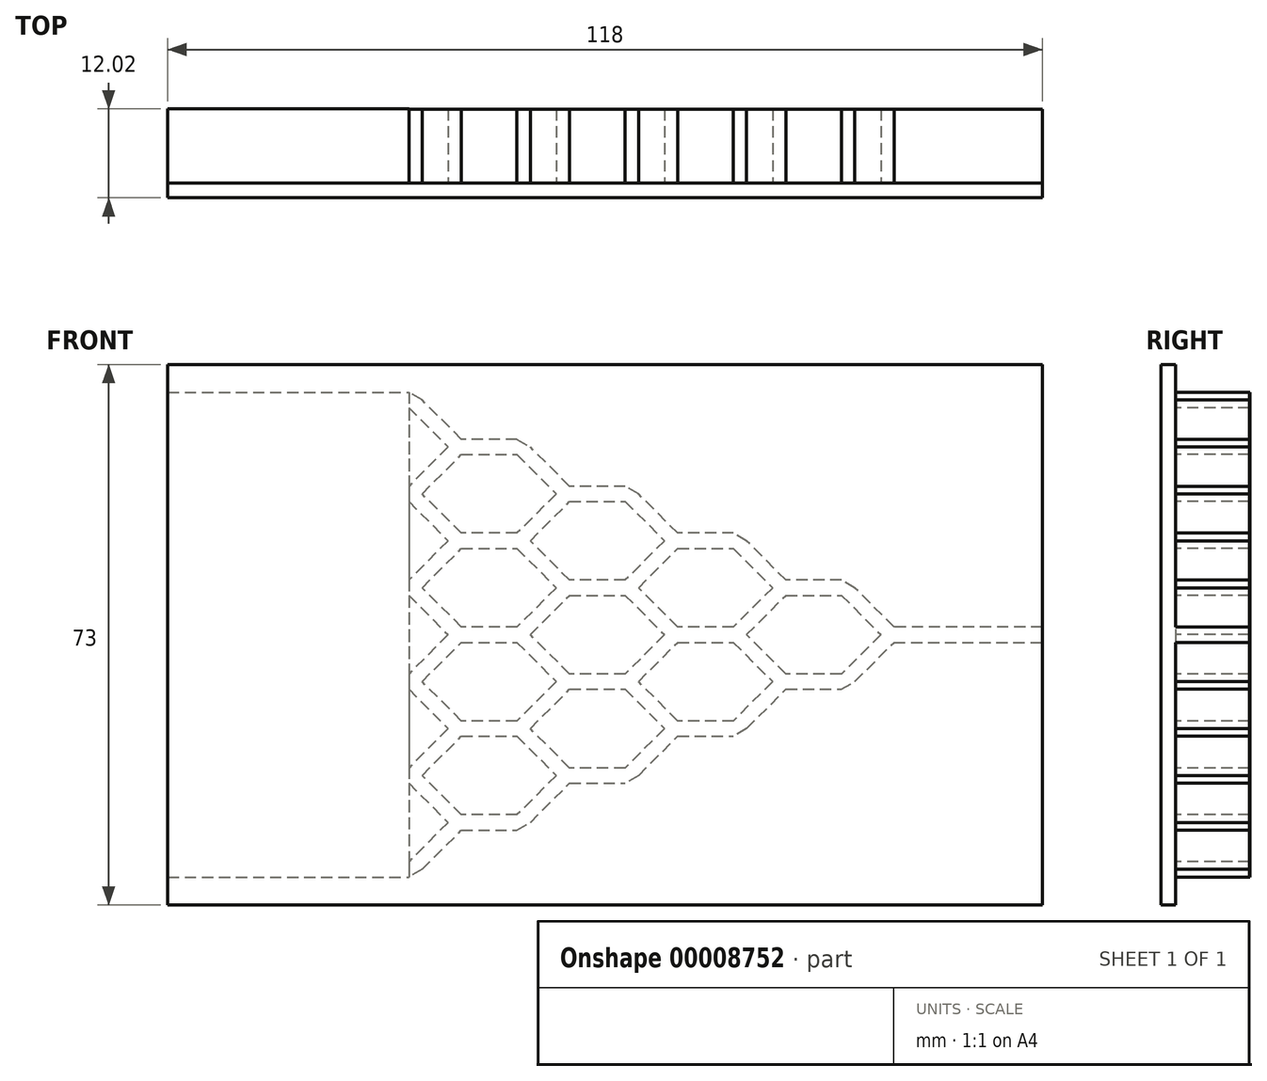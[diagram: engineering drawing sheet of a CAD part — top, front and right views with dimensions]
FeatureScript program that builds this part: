
annotation { "Feature Type Name" : "Feature", "Feature Type Description" : "" }
export const myFeature = defineFeature(function(context is Context, id is Id, definition is map)
    precondition{}
    {
        {
            var Q0;
            Q0=qCreatedBy(makeId("Front.planeOp"),FACE);
            var sketch = newSketch(context, id + "F0", { "sketchPlane" : qUnion([Q0])});
            skLineSegment(sketch, "E0.bottom", {"start": v(-59, 36.5) * mm, "end": v(59, 36.5) * mm});
            skLineSegment(sketch, "E0.top", {"start": v(-59, -36.5) * mm, "end": v(59, -36.5) * mm});
            skLineSegment(sketch, "E0.left", {"start": v(-59, 36.5) * mm, "end": v(-59, -36.5) * mm});
            skLineSegment(sketch, "E0.right", {"start": v(59, 36.5) * mm, "end": v(59, -36.5) * mm});
            skSolve(sketch);
        }
        {
            var Q0;
            Q0 = qSketchRegion(id + "F0", true);
            extrude(context, id + "F1", {"entities" : qUnion([Q0]), "depth" : 2 * mm});
        }
        {
            var Q0;
            Q0=makeQuery(id+"F1.opExtrude","CAP_FACE",FACE,{"disambiguationData":[OSD([sQuery(id+"F0.wireOp",EDGE,"E0.bottom"),sQuery(id+"F0.wireOp",EDGE,"E0.top"),sQuery(id+"F0.wireOp",EDGE,"E0.left"),sQuery(id+"F0.wireOp",EDGE,"E0.right")])],"isStart":true});
            var sketch = newSketch(context, id + "F2", { "sketchPlane" : qUnion([Q0])});
            skLineSegment(sketch, "E1", {"start": v(-59, 1.04) * mm, "end": v(-39, 1.04) * mm});
            skLineSegment(sketch, "E2", {"start": v(-39, 1.04) * mm, "end": v(-33.7, 6.34) * mm});
            skLineSegment(sketch, "E3", {"start": v(-31.9, 5.3) * mm, "end": v(-37.2, 0) * mm});
            skLineSegment(sketch, "E4", {"start": v(-37.2, 0) * mm, "end": v(-31.9, -5.3) * mm});
            skLineSegment(sketch, "E5", {"start": v(-33.7, -6.34) * mm, "end": v(-39, -1.04) * mm});
            skLineSegment(sketch, "E6", {"start": v(-39, -1.04) * mm, "end": v(-59, -1.04) * mm});
            skLineSegment(sketch, "E7", {"start": v(22.8, 0) * mm, "end": v(-82.74, 0) * mm, "construction": true});
            skLineSegment(sketch, "E8", {"start": v(-39, 1.04) * mm, "end": v(-37.2, 0) * mm, "construction": true});
            skLineSegment(sketch, "E9", {"start": v(-37.2, 0) * mm, "end": v(-39, -1.04) * mm, "construction": true});
            skLineSegment(sketch, "E10", {"start": v(-39, 1.04) * mm, "end": v(-39, -1.04) * mm, "construction": true});
            skLineSegment(sketch, "E11", {"start": v(-31.9, 5.3) * mm, "end": v(-33.7, 6.34) * mm, "construction": true});
            skLineSegment(sketch, "E12", {"start": v(-31.9, -5.3) * mm, "end": v(-33.7, -6.34) * mm, "construction": true});
            skLineSegment(sketch, "E13", {"start": v(23.45, 0) * mm, "end": v(-32.5, 0) * mm, "construction": true});
            skLineSegment(sketch, "E14", {"start": v(-59, 1.04) * mm, "end": v(-59, -1.04) * mm, "construction": true});
            skLineSegment(sketch, "E15", {"start": v(-31.9, 7.37) * mm, "end": v(-24.4, 7.37) * mm});
            skLineSegment(sketch, "E16", {"start": v(-24.4, 7.37) * mm, "end": v(-19.1, 12.68) * mm});
            skLineSegment(sketch, "E17", {"start": v(-17.3, 11.64) * mm, "end": v(-22.61, 6.34) * mm});
            skLineSegment(sketch, "E18", {"start": v(-22.61, 6.34) * mm, "end": v(-17.3, 1.04) * mm});
            skLineSegment(sketch, "E19", {"start": v(-19.1, 0) * mm, "end": v(-24.4, 5.3) * mm});
            skLineSegment(sketch, "E20", {"start": v(-24.4, 5.3) * mm, "end": v(-31.9, 5.3) * mm});
            skLineSegment(sketch, "E21", {"start": v(-24.4, 7.37) * mm, "end": v(-22.61, 6.34) * mm, "construction": true});
            skLineSegment(sketch, "E22", {"start": v(-22.61, 6.34) * mm, "end": v(-24.4, 5.3) * mm, "construction": true});
            skLineSegment(sketch, "E23", {"start": v(-24.4, 7.37) * mm, "end": v(-24.4, 5.3) * mm, "construction": true});
            skLineSegment(sketch, "E24", {"start": v(-17.3, 11.64) * mm, "end": v(-19.1, 12.68) * mm, "construction": true});
            skLineSegment(sketch, "E25", {"start": v(-17.3, 1.04) * mm, "end": v(-19.1, 0) * mm, "construction": true});
            skLineSegment(sketch, "E26", {"start": v(-31.9, -5.3) * mm, "end": v(-24.4, -5.3) * mm});
            skLineSegment(sketch, "E27", {"start": v(-24.4, -5.3) * mm, "end": v(-19.1, 0) * mm});
            skLineSegment(sketch, "E28", {"start": v(-17.3, -1.04) * mm, "end": v(-22.61, -6.34) * mm});
            skLineSegment(sketch, "E29", {"start": v(-22.61, -6.34) * mm, "end": v(-17.3, -11.64) * mm});
            skLineSegment(sketch, "E30", {"start": v(-19.1, -12.68) * mm, "end": v(-24.4, -7.37) * mm});
            skLineSegment(sketch, "E31", {"start": v(-24.4, -7.37) * mm, "end": v(-31.9, -7.37) * mm});
            skLineSegment(sketch, "E32", {"start": v(22.76, -6.34) * mm, "end": v(-25.18, -6.34) * mm, "construction": true});
            skLineSegment(sketch, "E33", {"start": v(-24.4, -5.3) * mm, "end": v(-22.61, -6.34) * mm, "construction": true});
            skLineSegment(sketch, "E34", {"start": v(-22.61, -6.34) * mm, "end": v(-24.4, -7.37) * mm, "construction": true});
            skLineSegment(sketch, "E35", {"start": v(-24.4, -5.3) * mm, "end": v(-24.4, -7.37) * mm, "construction": true});
            skLineSegment(sketch, "E36", {"start": v(-17.3, -1.04) * mm, "end": v(-19.1, 0) * mm, "construction": true});
            skLineSegment(sketch, "E37", {"start": v(-17.3, -11.64) * mm, "end": v(-19.1, -12.68) * mm, "construction": true});
            skLineSegment(sketch, "E38", {"start": v(-17.3, 13.71) * mm, "end": v(-9.8, 13.71) * mm});
            skLineSegment(sketch, "E39", {"start": v(-9.8, 13.71) * mm, "end": v(-4.5, 19.02) * mm});
            skLineSegment(sketch, "E40", {"start": v(-2.71, 17.98) * mm, "end": v(-8.01, 12.68) * mm});
            skLineSegment(sketch, "E41", {"start": v(-8.01, 12.68) * mm, "end": v(-2.71, 7.37) * mm});
            skLineSegment(sketch, "E42", {"start": v(-4.5, 6.34) * mm, "end": v(-9.8, 11.64) * mm});
            skLineSegment(sketch, "E43", {"start": v(-9.8, 11.64) * mm, "end": v(-17.3, 11.64) * mm});
            skLineSegment(sketch, "E44", {"start": v(19.34, 12.68) * mm, "end": v(-28.6, 12.68) * mm, "construction": true});
            skLineSegment(sketch, "E45", {"start": v(-9.8, 13.71) * mm, "end": v(-8.01, 12.68) * mm, "construction": true});
            skLineSegment(sketch, "E46", {"start": v(-8.01, 12.68) * mm, "end": v(-9.8, 11.64) * mm, "construction": true});
            skLineSegment(sketch, "E47", {"start": v(-9.8, 13.71) * mm, "end": v(-9.8, 11.64) * mm, "construction": true});
            skLineSegment(sketch, "E48", {"start": v(-2.71, 17.98) * mm, "end": v(-4.5, 19.02) * mm, "construction": true});
            skLineSegment(sketch, "E49", {"start": v(-2.71, 7.37) * mm, "end": v(-4.5, 6.34) * mm, "construction": true});
            skLineSegment(sketch, "E50", {"start": v(-17.3, 1.04) * mm, "end": v(-9.8, 1.04) * mm});
            skLineSegment(sketch, "E51", {"start": v(-9.8, 1.04) * mm, "end": v(-4.5, 6.34) * mm});
            skLineSegment(sketch, "E52", {"start": v(-2.71, 5.3) * mm, "end": v(-8.01, 0) * mm});
            skLineSegment(sketch, "E53", {"start": v(-8.01, 0) * mm, "end": v(-2.71, -5.3) * mm});
            skLineSegment(sketch, "E54", {"start": v(-4.5, -6.34) * mm, "end": v(-9.8, -1.04) * mm});
            skLineSegment(sketch, "E55", {"start": v(-9.8, -1.04) * mm, "end": v(-17.3, -1.04) * mm});
            skLineSegment(sketch, "E56", {"start": v(23.63, 0) * mm, "end": v(-24.3, 0) * mm, "construction": true});
            skLineSegment(sketch, "E57", {"start": v(-9.8, 1.04) * mm, "end": v(-8.01, 0) * mm, "construction": true});
            skLineSegment(sketch, "E58", {"start": v(-8.01, 0) * mm, "end": v(-9.8, -1.04) * mm, "construction": true});
            skLineSegment(sketch, "E59", {"start": v(-9.8, 1.04) * mm, "end": v(-9.8, -1.04) * mm, "construction": true});
            skLineSegment(sketch, "E60", {"start": v(-2.71, 5.3) * mm, "end": v(-4.5, 6.34) * mm, "construction": true});
            skLineSegment(sketch, "E61", {"start": v(-2.71, -5.3) * mm, "end": v(-4.5, -6.34) * mm, "construction": true});
            skLineSegment(sketch, "E62", {"start": v(-17.3, -11.64) * mm, "end": v(-9.8, -11.64) * mm});
            skLineSegment(sketch, "E63", {"start": v(-9.8, -11.64) * mm, "end": v(-4.5, -6.34) * mm});
            skLineSegment(sketch, "E64", {"start": v(-2.71, -7.37) * mm, "end": v(-8.01, -12.68) * mm});
            skLineSegment(sketch, "E65", {"start": v(-8.01, -12.68) * mm, "end": v(-2.71, -17.98) * mm});
            skLineSegment(sketch, "E66", {"start": v(-4.5, -19.02) * mm, "end": v(-9.8, -13.71) * mm});
            skLineSegment(sketch, "E67", {"start": v(-9.8, -13.71) * mm, "end": v(-17.3, -13.71) * mm});
            skLineSegment(sketch, "E68", {"start": v(17.06, -12.68) * mm, "end": v(-30.88, -12.68) * mm, "construction": true});
            skLineSegment(sketch, "E69", {"start": v(-9.8, -11.64) * mm, "end": v(-8.01, -12.68) * mm, "construction": true});
            skLineSegment(sketch, "E70", {"start": v(-8.01, -12.68) * mm, "end": v(-9.8, -13.71) * mm, "construction": true});
            skLineSegment(sketch, "E71", {"start": v(-9.8, -11.64) * mm, "end": v(-9.8, -13.71) * mm, "construction": true});
            skLineSegment(sketch, "E72", {"start": v(-2.71, -7.37) * mm, "end": v(-4.5, -6.34) * mm, "construction": true});
            skLineSegment(sketch, "E73", {"start": v(-2.71, -17.98) * mm, "end": v(-4.5, -19.02) * mm, "construction": true});
            skLineSegment(sketch, "E74", {"start": v(-31.9, -7.37) * mm, "end": v(-33.7, -6.34) * mm});
            skLineSegment(sketch, "E75", {"start": v(-2.71, 20.05) * mm, "end": v(4.79, 20.05) * mm});
            skLineSegment(sketch, "E76", {"start": v(4.79, 20.05) * mm, "end": v(10.1, 25.35) * mm});
            skLineSegment(sketch, "E77", {"start": v(11.89, 24.32) * mm, "end": v(6.58, 19.02) * mm});
            skLineSegment(sketch, "E78", {"start": v(6.58, 19.02) * mm, "end": v(11.89, 13.71) * mm});
            skLineSegment(sketch, "E79", {"start": v(10.1, 12.68) * mm, "end": v(4.79, 17.98) * mm});
            skLineSegment(sketch, "E80", {"start": v(4.79, 17.98) * mm, "end": v(-2.71, 17.98) * mm});
            skLineSegment(sketch, "E81", {"start": v(36.18, 19.02) * mm, "end": v(-11.76, 19.02) * mm, "construction": true});
            skLineSegment(sketch, "E82", {"start": v(4.79, 20.05) * mm, "end": v(6.58, 19.02) * mm, "construction": true});
            skLineSegment(sketch, "E83", {"start": v(6.58, 19.02) * mm, "end": v(4.79, 17.98) * mm, "construction": true});
            skLineSegment(sketch, "E84", {"start": v(4.79, 20.05) * mm, "end": v(4.79, 17.98) * mm, "construction": true});
            skLineSegment(sketch, "E85", {"start": v(11.89, 24.32) * mm, "end": v(10.1, 25.35) * mm, "construction": true});
            skLineSegment(sketch, "E86", {"start": v(11.89, 13.71) * mm, "end": v(10.1, 12.68) * mm, "construction": true});
            skLineSegment(sketch, "E87", {"start": v(-2.71, -17.98) * mm, "end": v(4.79, -17.98) * mm});
            skLineSegment(sketch, "E88", {"start": v(4.79, -17.98) * mm, "end": v(10.1, -12.68) * mm});
            skLineSegment(sketch, "E89", {"start": v(11.89, -13.71) * mm, "end": v(6.58, -19.02) * mm});
            skLineSegment(sketch, "E90", {"start": v(6.58, -19.02) * mm, "end": v(11.89, -24.32) * mm});
            skLineSegment(sketch, "E91", {"start": v(10.1, -25.35) * mm, "end": v(4.79, -20.05) * mm});
            skLineSegment(sketch, "E92", {"start": v(4.79, -20.05) * mm, "end": v(-2.71, -20.05) * mm});
            skLineSegment(sketch, "E93", {"start": v(31.97, -19.02) * mm, "end": v(-15.97, -19.02) * mm, "construction": true});
            skLineSegment(sketch, "E94", {"start": v(4.79, -17.98) * mm, "end": v(6.58, -19.02) * mm, "construction": true});
            skLineSegment(sketch, "E95", {"start": v(6.58, -19.02) * mm, "end": v(4.79, -20.05) * mm, "construction": true});
            skLineSegment(sketch, "E96", {"start": v(4.79, -17.98) * mm, "end": v(4.79, -20.05) * mm, "construction": true});
            skLineSegment(sketch, "E97", {"start": v(11.89, -13.71) * mm, "end": v(10.1, -12.68) * mm, "construction": true});
            skLineSegment(sketch, "E98", {"start": v(11.89, -24.32) * mm, "end": v(10.1, -25.35) * mm, "construction": true});
            skLineSegment(sketch, "E99", {"start": v(-2.71, 7.37) * mm, "end": v(4.79, 7.37) * mm});
            skLineSegment(sketch, "E100", {"start": v(4.79, 7.37) * mm, "end": v(10.1, 12.68) * mm});
            skLineSegment(sketch, "E101", {"start": v(11.89, 11.64) * mm, "end": v(6.58, 6.34) * mm});
            skLineSegment(sketch, "E102", {"start": v(6.58, 6.34) * mm, "end": v(11.89, 1.04) * mm});
            skLineSegment(sketch, "E103", {"start": v(10.1, 0) * mm, "end": v(4.79, 5.3) * mm});
            skLineSegment(sketch, "E104", {"start": v(4.79, 5.3) * mm, "end": v(-2.71, 5.3) * mm});
            skLineSegment(sketch, "E105", {"start": v(22.04, 6.34) * mm, "end": v(-25.9, 6.34) * mm, "construction": true});
            skLineSegment(sketch, "E106", {"start": v(4.79, 7.37) * mm, "end": v(6.58, 6.34) * mm, "construction": true});
            skLineSegment(sketch, "E107", {"start": v(6.58, 6.34) * mm, "end": v(4.79, 5.3) * mm, "construction": true});
            skLineSegment(sketch, "E108", {"start": v(4.79, 7.37) * mm, "end": v(4.79, 5.3) * mm, "construction": true});
            skLineSegment(sketch, "E109", {"start": v(11.89, 11.64) * mm, "end": v(10.1, 12.68) * mm, "construction": true});
            skLineSegment(sketch, "E110", {"start": v(11.89, 1.04) * mm, "end": v(10.1, 0) * mm, "construction": true});
            skLineSegment(sketch, "E111", {"start": v(-2.71, -5.3) * mm, "end": v(4.79, -5.3) * mm});
            skLineSegment(sketch, "E112", {"start": v(4.79, -5.3) * mm, "end": v(10.1, 0) * mm});
            skLineSegment(sketch, "E113", {"start": v(11.89, -1.04) * mm, "end": v(6.58, -6.34) * mm});
            skLineSegment(sketch, "E114", {"start": v(6.58, -6.34) * mm, "end": v(11.89, -11.64) * mm});
            skLineSegment(sketch, "E115", {"start": v(10.1, -12.68) * mm, "end": v(4.79, -7.37) * mm});
            skLineSegment(sketch, "E116", {"start": v(4.79, -7.37) * mm, "end": v(-2.71, -7.37) * mm});
            skLineSegment(sketch, "E117", {"start": v(22.9, -6.34) * mm, "end": v(-25.04, -6.34) * mm, "construction": true});
            skLineSegment(sketch, "E118", {"start": v(4.79, -5.3) * mm, "end": v(6.58, -6.34) * mm, "construction": true});
            skLineSegment(sketch, "E119", {"start": v(6.58, -6.34) * mm, "end": v(4.79, -7.37) * mm, "construction": true});
            skLineSegment(sketch, "E120", {"start": v(4.79, -5.3) * mm, "end": v(4.79, -7.37) * mm, "construction": true});
            skLineSegment(sketch, "E121", {"start": v(11.89, -1.04) * mm, "end": v(10.1, 0) * mm, "construction": true});
            skLineSegment(sketch, "E122", {"start": v(11.89, -11.64) * mm, "end": v(10.1, -12.68) * mm, "construction": true});
            skLineSegment(sketch, "E123", {"start": v(-59, 1.04) * mm, "end": v(-59, -1.04) * mm});
            skLineSegment(sketch, "E124", {"start": v(-33.7, 6.34) * mm, "end": v(-31.9, 7.37) * mm});
            skLineSegment(sketch, "E125", {"start": v(-19.1, 12.68) * mm, "end": v(-17.3, 13.71) * mm});
            skLineSegment(sketch, "E126", {"start": v(-4.5, 19.02) * mm, "end": v(-2.71, 20.05) * mm});
            skLineSegment(sketch, "E127", {"start": v(-19.1, -12.68) * mm, "end": v(-17.3, -13.71) * mm});
            skLineSegment(sketch, "E128", {"start": v(-4.5, -19.02) * mm, "end": v(-2.71, -20.05) * mm});
            skLineSegment(sketch, "E129", {"start": v(9.88, -12.68) * mm, "end": v(-38.06, -12.68) * mm, "construction": true});
            skLineSegment(sketch, "E130", {"start": v(21.96, 12.68) * mm, "end": v(-25.98, 12.68) * mm, "construction": true});
            skLineSegment(sketch, "E131", {"start": v(11.89, 26.39) * mm, "end": v(10.1, 25.35) * mm});
            skLineSegment(sketch, "E132", {"start": v(11.89, -26.39) * mm, "end": v(10.1, -25.35) * mm});
            skLineSegment(sketch, "E133", {"start": v(11.89, 13.71) * mm, "end": v(19.39, 13.71) * mm});
            skLineSegment(sketch, "E134", {"start": v(19.39, 13.71) * mm, "end": v(24.69, 19.02) * mm});
            skLineSegment(sketch, "E135", {"start": v(26.48, 17.98) * mm, "end": v(21.18, 12.68) * mm});
            skLineSegment(sketch, "E136", {"start": v(21.18, 12.68) * mm, "end": v(26.48, 7.37) * mm});
            skLineSegment(sketch, "E137", {"start": v(24.69, 6.34) * mm, "end": v(19.39, 11.64) * mm});
            skLineSegment(sketch, "E138", {"start": v(19.39, 11.64) * mm, "end": v(11.89, 11.64) * mm});
            skLineSegment(sketch, "E139", {"start": v(23.9, 12.68) * mm, "end": v(-24.04, 12.68) * mm, "construction": true});
            skLineSegment(sketch, "E140", {"start": v(19.39, 13.71) * mm, "end": v(21.18, 12.68) * mm, "construction": true});
            skLineSegment(sketch, "E141", {"start": v(21.18, 12.68) * mm, "end": v(19.39, 11.64) * mm, "construction": true});
            skLineSegment(sketch, "E142", {"start": v(19.39, 13.71) * mm, "end": v(19.39, 11.64) * mm, "construction": true});
            skLineSegment(sketch, "E143", {"start": v(26.48, 17.98) * mm, "end": v(24.69, 19.02) * mm, "construction": true});
            skLineSegment(sketch, "E144", {"start": v(26.48, 7.37) * mm, "end": v(24.69, 6.34) * mm, "construction": true});
            skLineSegment(sketch, "E145", {"start": v(11.89, 1.04) * mm, "end": v(19.39, 1.04) * mm});
            skLineSegment(sketch, "E146", {"start": v(19.39, 1.04) * mm, "end": v(24.69, 6.34) * mm});
            skLineSegment(sketch, "E147", {"start": v(26.48, 5.3) * mm, "end": v(21.18, 0) * mm});
            skLineSegment(sketch, "E148", {"start": v(21.18, 0) * mm, "end": v(26.48, -5.3) * mm});
            skLineSegment(sketch, "E149", {"start": v(24.69, -6.34) * mm, "end": v(19.39, -1.04) * mm});
            skLineSegment(sketch, "E150", {"start": v(19.39, -1.04) * mm, "end": v(11.89, -1.04) * mm});
            skLineSegment(sketch, "E151", {"start": v(17.53, 0) * mm, "end": v(-30.4, 0) * mm, "construction": true});
            skLineSegment(sketch, "E152", {"start": v(19.39, 1.04) * mm, "end": v(21.18, 0) * mm, "construction": true});
            skLineSegment(sketch, "E153", {"start": v(21.18, 0) * mm, "end": v(19.39, -1.04) * mm, "construction": true});
            skLineSegment(sketch, "E154", {"start": v(19.39, 1.04) * mm, "end": v(19.39, -1.04) * mm, "construction": true});
            skLineSegment(sketch, "E155", {"start": v(26.48, 5.3) * mm, "end": v(24.69, 6.34) * mm, "construction": true});
            skLineSegment(sketch, "E156", {"start": v(26.48, -5.3) * mm, "end": v(24.69, -6.34) * mm, "construction": true});
            skLineSegment(sketch, "E157", {"start": v(11.89, -11.64) * mm, "end": v(19.39, -11.64) * mm});
            skLineSegment(sketch, "E158", {"start": v(19.39, -11.64) * mm, "end": v(24.69, -6.34) * mm});
            skLineSegment(sketch, "E159", {"start": v(26.48, -7.37) * mm, "end": v(21.18, -12.68) * mm});
            skLineSegment(sketch, "E160", {"start": v(21.18, -12.68) * mm, "end": v(26.48, -17.98) * mm});
            skLineSegment(sketch, "E161", {"start": v(24.69, -19.02) * mm, "end": v(19.39, -13.71) * mm});
            skLineSegment(sketch, "E162", {"start": v(19.39, -13.71) * mm, "end": v(11.89, -13.71) * mm});
            skLineSegment(sketch, "E163", {"start": v(18.65, -12.68) * mm, "end": v(-29.3, -12.68) * mm, "construction": true});
            skLineSegment(sketch, "E164", {"start": v(19.39, -11.64) * mm, "end": v(21.18, -12.68) * mm, "construction": true});
            skLineSegment(sketch, "E165", {"start": v(21.18, -12.68) * mm, "end": v(19.39, -13.71) * mm, "construction": true});
            skLineSegment(sketch, "E166", {"start": v(19.39, -11.64) * mm, "end": v(19.39, -13.71) * mm, "construction": true});
            skLineSegment(sketch, "E167", {"start": v(26.48, -7.37) * mm, "end": v(24.69, -6.34) * mm, "construction": true});
            skLineSegment(sketch, "E168", {"start": v(26.48, -17.98) * mm, "end": v(24.69, -19.02) * mm, "construction": true});
            skLineSegment(sketch, "E169", {"start": v(-17.3, 1.04) * mm, "end": v(-17.3, -1.04) * mm, "construction": true});
            skLineSegment(sketch, "E170", {"start": v(11.89, 26.39) * mm, "end": v(19.39, 26.39) * mm});
            skLineSegment(sketch, "E171", {"start": v(19.39, 26.39) * mm, "end": v(24.69, 31.7) * mm});
            skLineSegment(sketch, "E172", {"start": v(26.48, 30.66) * mm, "end": v(21.18, 25.35) * mm});
            skLineSegment(sketch, "E173", {"start": v(21.18, 25.35) * mm, "end": v(26.48, 20.05) * mm});
            skLineSegment(sketch, "E174", {"start": v(24.69, 19.02) * mm, "end": v(19.39, 24.32) * mm});
            skLineSegment(sketch, "E175", {"start": v(19.39, 24.32) * mm, "end": v(11.89, 24.32) * mm});
            skLineSegment(sketch, "E176", {"start": v(23.62, 25.35) * mm, "end": v(-24.32, 25.35) * mm, "construction": true});
            skLineSegment(sketch, "E177", {"start": v(19.39, 26.39) * mm, "end": v(21.18, 25.35) * mm, "construction": true});
            skLineSegment(sketch, "E178", {"start": v(21.18, 25.35) * mm, "end": v(19.39, 24.32) * mm, "construction": true});
            skLineSegment(sketch, "E179", {"start": v(19.39, 26.39) * mm, "end": v(19.39, 24.32) * mm, "construction": true});
            skLineSegment(sketch, "E180", {"start": v(26.48, 30.66) * mm, "end": v(24.69, 31.7) * mm, "construction": true});
            skLineSegment(sketch, "E181", {"start": v(26.48, 20.05) * mm, "end": v(24.69, 19.02) * mm, "construction": true});
            skLineSegment(sketch, "E182", {"start": v(11.89, -24.32) * mm, "end": v(19.39, -24.32) * mm});
            skLineSegment(sketch, "E183", {"start": v(19.39, -24.32) * mm, "end": v(24.69, -19.02) * mm});
            skLineSegment(sketch, "E184", {"start": v(26.48, -20.05) * mm, "end": v(21.18, -25.35) * mm});
            skLineSegment(sketch, "E185", {"start": v(21.18, -25.35) * mm, "end": v(26.48, -30.66) * mm});
            skLineSegment(sketch, "E186", {"start": v(24.69, -31.7) * mm, "end": v(19.39, -26.39) * mm});
            skLineSegment(sketch, "E187", {"start": v(19.39, -26.39) * mm, "end": v(11.89, -26.39) * mm});
            skLineSegment(sketch, "E188", {"start": v(22.24, -25.35) * mm, "end": v(-25.7, -25.35) * mm, "construction": true});
            skLineSegment(sketch, "E189", {"start": v(19.39, -24.32) * mm, "end": v(21.18, -25.35) * mm, "construction": true});
            skLineSegment(sketch, "E190", {"start": v(21.18, -25.35) * mm, "end": v(19.39, -26.39) * mm, "construction": true});
            skLineSegment(sketch, "E191", {"start": v(19.39, -24.32) * mm, "end": v(19.39, -26.39) * mm, "construction": true});
            skLineSegment(sketch, "E192", {"start": v(26.48, -20.05) * mm, "end": v(24.69, -19.02) * mm, "construction": true});
            skLineSegment(sketch, "E193", {"start": v(26.48, -30.66) * mm, "end": v(24.69, -31.7) * mm, "construction": true});
            skLineSegment(sketch, "E194", {"start": v(24.69, 31.7) * mm, "end": v(26.48, 32.73) * mm});
            skLineSegment(sketch, "E195", {"start": v(26.48, 32.73) * mm, "end": v(26.48, 30.66) * mm});
            skLineSegment(sketch, "E196", {"start": v(26.48, 20.05) * mm, "end": v(26.48, 17.98) * mm});
            skLineSegment(sketch, "E197", {"start": v(26.48, 7.37) * mm, "end": v(26.48, 5.3) * mm});
            skLineSegment(sketch, "E198", {"start": v(26.48, -5.3) * mm, "end": v(26.48, -7.37) * mm});
            skLineSegment(sketch, "E199", {"start": v(26.48, -17.98) * mm, "end": v(26.48, -20.05) * mm});
            skLineSegment(sketch, "E200", {"start": v(24.69, -31.7) * mm, "end": v(26.48, -32.73) * mm});
            skLineSegment(sketch, "E201", {"start": v(26.48, -30.66) * mm, "end": v(26.48, -32.73) * mm});
            skSolve(sketch);
        }
        {
            var Q0;
            Q0=makeQuery(id+"F2.imprint","IMPRINT",FACE,{"disambiguationData":[TD([[makeQuery(id+"F2.imprint","IMPRINT",EDGE,{"derivedFrom":sQuery(id+"F2.wireOp",EDGE,"E1")}),-1.0]])]});
            extrude(context, id + "F3", {"entities" : qUnion([Q0]), "operationType" : NewBodyOperationType.ADD, "depth" : 9.95 * mm});
        }
        {
            var Q0;
            {var subQ0=sQuery(id+"F0.wireOp",EDGE,"E0.bottom");var subQ1=sQuery(id+"F0.wireOp",EDGE,"E0.top");var subQ2=sQuery(id+"F0.wireOp",EDGE,"E0.left");var subQ3=sQuery(id+"F0.wireOp",EDGE,"E0.right");Q0=makeQuery(id+"F3.boolean.opBoolean","SPLIT",FACE,{"disambiguationData":[TD([makeQuery(id+"F1.opExtrude","SWEPT_FACE",FACE,{"disambiguationData":[OSD([subQ0])]})])],"derivedFrom":makeQuery(id+"F1.opExtrude","CAP_FACE",FACE,{"disambiguationData":[OSD([subQ0,subQ1,subQ2,subQ3])],"isStart":true})});}
            var sketch = newSketch(context, id + "F4", { "sketchPlane" : qUnion([Q0])});
            skLineSegment(sketch, "E202.bottom", {"start": v(59, 32.73) * mm, "end": v(26.48, 32.73) * mm});
            skLineSegment(sketch, "E202.top", {"start": v(59, -32.73) * mm, "end": v(26.48, -32.73) * mm});
            skLineSegment(sketch, "E202.left", {"start": v(59, 32.73) * mm, "end": v(59, -32.73) * mm});
            skLineSegment(sketch, "E202.right", {"start": v(26.48, 32.73) * mm, "end": v(26.48, -32.73) * mm});
            skSolve(sketch);
        }
        {
            var Q0;
            Q0 = qSketchRegion(id + "F4", true);
            extrude(context, id + "F5", {"entities" : qUnion([Q0]), "operationType" : NewBodyOperationType.ADD, "depth" : 10.02 * mm});
        }
    });
